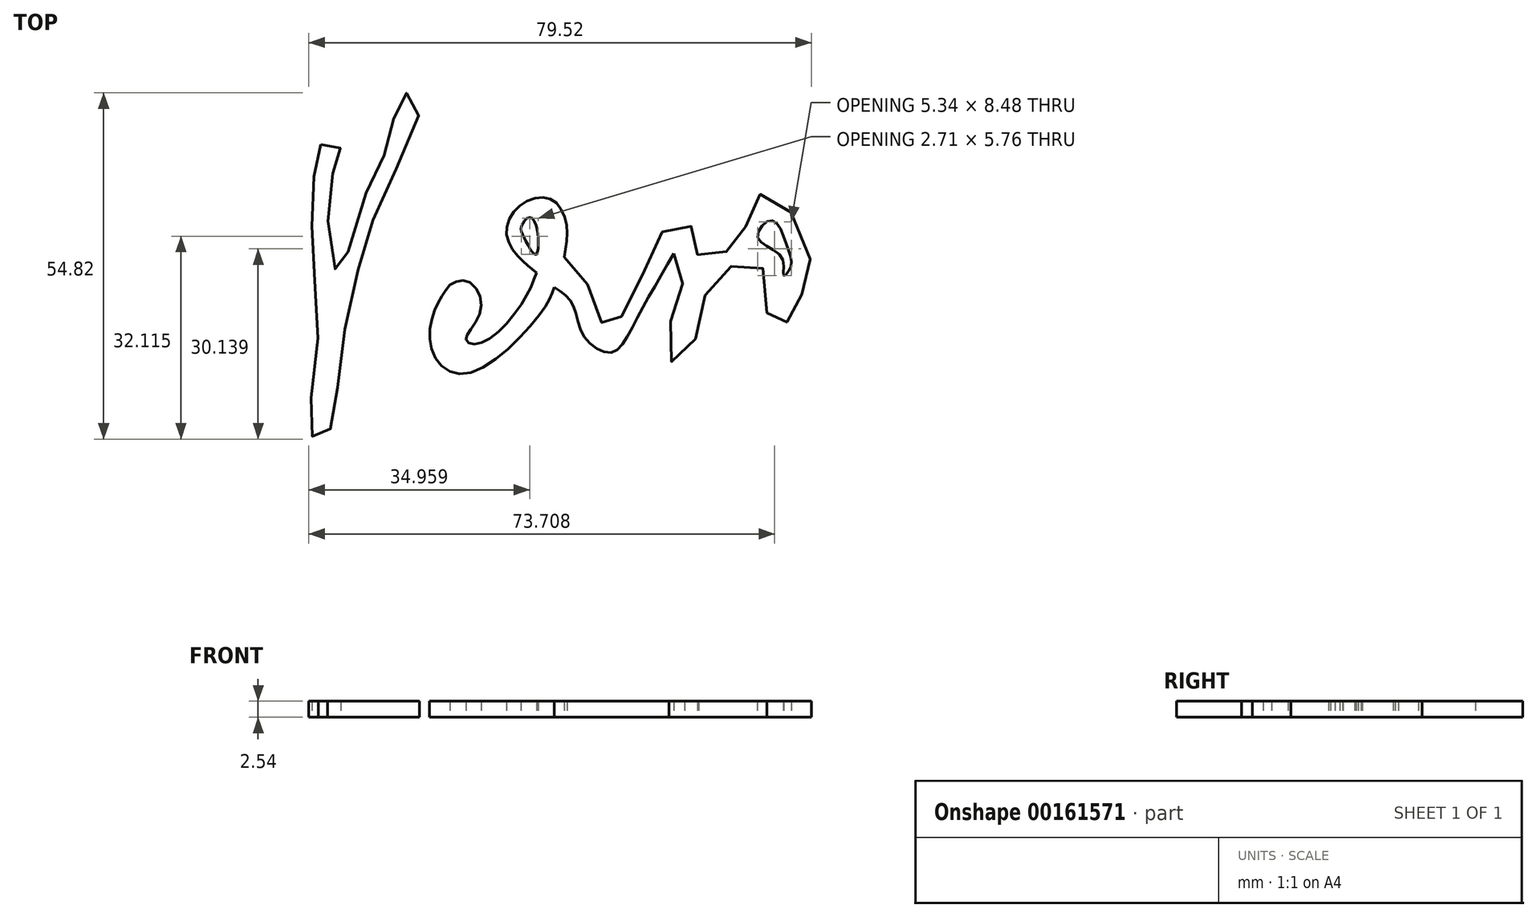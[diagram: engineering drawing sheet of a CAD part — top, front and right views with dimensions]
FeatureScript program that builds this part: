
annotation { "Feature Type Name" : "Feature", "Feature Type Description" : "" }
export const myFeature = defineFeature(function(context is Context, id is Id, definition is map)
    precondition{}
    {
        {
            var Q0;
            Q0=qCreatedBy(makeId("Top.planeOp"),FACE);
            var sketch = newSketch(context, id + "F0", { "sketchPlane" : qUnion([Q0])});
            skFitSpline(sketch, "E0", {"points": [v(-43.69, 4.8) * mm, v(-44.78, 0) * mm, v(-45.02, -11.97) * mm, v(-44.17, -26.91) * mm, v(-45.5, -40.16) * mm, v(-44.3, -41.86) * mm, v(-42.1, -40.16) * mm, v(-40.77, -30.44) * mm, v(-37.49, -13.91) * mm, v(-33.24, -2) * mm, v(-28.13, 11.12) * mm, v(-30.08, 12.94) * mm, v(-31.78, 10.4) * mm, v(-33.36, 3.83) * mm, v(-36.76, -3.58) * mm, v(-40.77, -15.5) * mm, v(-41.74, -13.79) * mm, v(-42.23, -1.15) * mm, v(-40.65, 2.62) * mm, v(-41.13, 5.17) * mm, v(-43.69, 4.8) * mm]});
            skFitSpline(sketch, "E1", {"points": [v(-23.27, -17.44) * mm, v(-25.34, -20.72) * mm, v(-26.19, -27.52) * mm, v(-20.96, -31.53) * mm, v(-8.81, -21.8) * mm, v(-6.74, -17.8) * mm], "startDerivative": vector(-14.47, -19.08) * mm, "endDerivative": vector(7.03, 20.44) * mm});
            skFitSpline(sketch, "E2", {"points": [v(-6.74, -17.8) * mm, v(-3.83, -20.47) * mm, v(-2.13, -25.46) * mm, v(2.25, -28.13) * mm, v(6.01, -23.39) * mm, v(12.21, -12.45) * mm], "startDerivative": vector(21.78, -14.05) * mm, "endDerivative": vector(23.64, 40.23) * mm});
            skFitSpline(sketch, "E3", {"points": [v(12.21, -12.45) * mm, v(13.91, -15.61) * mm, v(12.46, -19.99) * mm, v(11.48, -25.58) * mm, v(12.1, -29.83) * mm, v(15.13, -27.04) * mm, v(16.83, -20.23) * mm, v(19.14, -15.98) * mm, v(24, -13.67) * mm, v(26.55, -15.37) * mm, v(26.92, -22.17) * mm, v(27.52, -23.63) * mm, v(31.17, -22.66) * mm, v(32.26, -19.38) * mm, v(33.84, -16.1) * mm, v(32.14, -8.56) * mm, v(28.25, -3.46) * mm, v(24.97, -3.58) * mm, v(23.51, -8.32) * mm, v(22.66, -10.5) * mm, v(17.8, -13.3) * mm, v(15.98, -12.82) * mm, v(16.1, -10.5) * mm, v(14.16, -7.71) * mm, v(10.88, -8.44) * mm, v(9.05, -12.09) * mm, v(4.8, -20.47) * mm, v(2.61, -24.12) * mm, v(0.91, -23.63) * mm, v(-0.18, -19.74) * mm, v(-4.56, -13.55) * mm, v(-5.17, -13.06) * mm], "startDerivative": vector(82.26, -99.81) * mm, "endDerivative": vector(-32.12, 20.14) * mm});
            skFitSpline(sketch, "E4", {"points": [v(-5.17, -13.06) * mm, v(-4.8, -7.84) * mm, v(-7.35, -3.82) * mm, v(-12.21, -4.92) * mm, v(-14.28, -9.54) * mm, v(-11.73, -13.67) * mm, v(-9.54, -15.5) * mm], "startDerivative": vector(5.6, 29.1) * mm, "endDerivative": vector(15.71, -11.83) * mm});
            skFitSpline(sketch, "E5", {"points": [v(-9.54, -15.5) * mm, v(-11.12, -19.14) * mm, v(-15.98, -25.21) * mm, v(-19.75, -26.8) * mm, v(-20.72, -26.06) * mm, v(-19.75, -24.24) * mm, v(-18.29, -19.99) * mm, v(-20.6, -16.83) * mm, v(-23.27, -17.44) * mm], "startDerivative": vector(-9.04, -25.38) * mm, "endDerivative": vector(-24.35, -12.23) * mm});
            skFitSpline(sketch, "E6", {"points": [v(-10.23, -6.86) * mm, v(-9.54, -12.57) * mm, v(-11.36, -10.27) * mm, v(-11.85, -7.96) * mm, v(-10.23, -6.86) * mm]});
            skFitSpline(sketch, "E7", {"points": [v(25.46, -9.9) * mm, v(27.65, -7.23) * mm, v(30.08, -11.24) * mm, v(30.68, -14.64) * mm, v(29.59, -15.98) * mm, v(29.35, -13.18) * mm, v(25.46, -9.9) * mm]});
            skFitSpline(sketch, "E8", {"points": [v(78.31, -9.28) * mm, v(77.05, -12.2) * mm, v(73.37, -11.94) * mm, v(69.83, -5.86) * mm, v(69.83, -0.16) * mm, v(67.93, 1.1) * mm, v(67.93, 4.15) * mm, v(69.83, 6.43) * mm, v(69.57, 9.47) * mm, v(71.85, 24.28) * mm, v(77.93, 39.86) * mm, v(81.86, 41.13) * mm, v(84.14, 37.7) * mm, v(83.25, 25.93) * mm, v(75.9, 10.6) * mm, v(72.74, 5.8) * mm], "startDerivative": vector(-14.94, -73.82) * mm, "endDerivative": vector(-43.32, -62.37) * mm});
            skFitSpline(sketch, "E9", {"points": [v(72.74, 5.8) * mm, v(72.61, -0.41) * mm, v(74.26, -8.01) * mm, v(77.05, -8.52) * mm, v(78.44, -8.14) * mm, v(78.31, -9.28) * mm], "startDerivative": vector(-1.12, -20.77) * mm, "endDerivative": vector(-3.7, -13.08) * mm});
            skFitSpline(sketch, "E10", {"points": [v(80.21, 36.44) * mm, v(75.9, 25.93) * mm, v(73.25, 15.3) * mm, v(73.25, 12.5) * mm, v(75.4, 14.78) * mm, v(79.33, 22.9) * mm, v(81.22, 31.88) * mm, v(81.48, 36.95) * mm, v(80.21, 36.44) * mm]});
            skFitSpline(sketch, "E11", {"points": [v(95.92, 34.42) * mm, v(96.8, 32.77) * mm, v(96.55, 28.59) * mm, v(97.82, 28.2) * mm, v(99.59, 30.49) * mm, v(99.08, 32.52) * mm, v(99.08, 35.94) * mm, v(96.8, 36.32) * mm, v(95.92, 34.42) * mm]});
            skFitSpline(sketch, "E12", {"points": [v(102.88, 11.74) * mm, v(100.35, 6.05) * mm, v(99.84, -2.44) * mm, v(102.5, -4.6) * mm, v(105.8, -2.44) * mm, v(107.82, 2.63) * mm, v(108.58, 2.25) * mm, v(112, 0.35) * mm, v(115.67, 0.98) * mm, v(122, 9.34) * mm], "startDerivative": vector(-21.7, -39.66) * mm, "endDerivative": vector(39, 63) * mm});
            skFitSpline(sketch, "E13", {"points": [v(102.88, 11.74) * mm, v(102.5, 13.14) * mm, v(103.52, 13.26) * mm], "startDerivative": vector(-1.5, 3.19) * mm, "endDerivative": vector(2.88, -0.25) * mm});
            skFitSpline(sketch, "E14", {"points": [v(103.52, 13.26) * mm, v(106.94, 18.08) * mm, v(109.09, 17.82) * mm, v(109.34, 11.62) * mm, v(110.48, 6.68) * mm, v(114.28, 4.65) * mm, v(117.2, 7.82) * mm, v(120.49, 12.12) * mm], "startDerivative": vector(19.66, 38.15) * mm, "endDerivative": vector(22.24, 26.78) * mm});
            skFitSpline(sketch, "E15", {"points": [v(139.1, 26.7) * mm, v(139.06, 35.98) * mm, v(141.28, 45.9) * mm, v(143.5, 48.46) * mm, v(146.87, 48) * mm, v(147.7, 40.65) * mm, v(143.73, 28.87) * mm, v(141.86, 25.02) * mm, v(143.5, 24.79) * mm, v(147.46, 27.47) * mm, v(152.94, 29.1) * mm, v(155.39, 28.17) * mm, v(154.92, 25.84) * mm, v(153.17, 26.07) * mm, v(148.62, 24.44) * mm, v(146.64, 21.87) * mm, v(145, 21.17) * mm, v(142.56, 17.68) * mm, v(141.98, 10.1) * mm, v(139.53, 1) * mm, v(138.36, 2.29) * mm, v(136.61, 2.75) * mm, v(136.5, 9.28) * mm, v(138.36, 17.91) * mm, v(137.43, 18.6) * mm, v(132.53, 11.61) * mm, v(127.52, 7.77) * mm, v(124.49, 7.88) * mm, v(122, 9.34) * mm], "startDerivative": vector(-11.09, 174.57) * mm, "endDerivative": vector(-84.35, 59.96) * mm});
            skFitSpline(sketch, "E16", {"points": [v(104.44, 7.77) * mm, v(102.92, 2.99) * mm, v(103.15, 1.12) * mm, v(105.25, 3.45) * mm, v(106.18, 6.37) * mm, v(104.44, 7.77) * mm]});
            skFitSpline(sketch, "E17", {"points": [v(107.47, 13.48) * mm, v(106.23, 12.47) * mm, v(107.4, 10.41) * mm, v(107.47, 13.48) * mm]});
            skFitSpline(sketch, "E18", {"points": [v(126.7, 36.33) * mm, v(124.6, 33.18) * mm, v(123.2, 17.91) * mm, v(125.07, 19.9) * mm, v(129.15, 29.57) * mm, v(130.79, 34.12) * mm, v(128.8, 37.26) * mm, v(126.7, 36.33) * mm]});
            skFitSpline(sketch, "E19", {"points": [v(143.73, 39.83) * mm, v(142.44, 37.61) * mm, v(142.44, 35.4) * mm, v(144.08, 37.5) * mm, v(143.73, 39.83) * mm]});
            skFitSpline(sketch, "E20", {"points": [v(152.82, 17.56) * mm, v(150.96, 16.98) * mm, v(150.26, 11.03) * mm, v(151.77, 6.25) * mm, v(155.39, 6.6) * mm, v(157.25, 6.37) * mm, v(158.3, 8.47) * mm, v(161.57, 12.55) * mm, v(162.85, 21.4) * mm, v(165.86, 21.91) * mm, v(162.61, 24.9) * mm, v(160.98, 23.86) * mm, v(158.18, 24.2) * mm, v(154.8, 22) * mm, v(154.4, 19) * mm, v(158.65, 21.17) * mm, v(159.93, 16.98) * mm, v(155.97, 11.15) * mm, v(153.4, 11.15) * mm, v(153.4, 14.76) * mm, v(154.8, 16.28) * mm, v(154.45, 17.56) * mm, v(152.82, 17.56) * mm]});
            skFitSpline(sketch, "E21", {"points": [v(139.1, 26.7) * mm, v(134.3, 19.3) * mm, v(128.9, 12.54) * mm, v(125.65, 11.96) * mm, v(125.07, 13.65) * mm, v(128.45, 21.51) * mm, v(132.16, 28.6) * mm, v(133.4, 36.86) * mm, v(129.36, 40.5) * mm, v(124.55, 38.62) * mm, v(120.71, 26.98) * mm, v(120.71, 17.87) * mm, v(120.49, 12.12) * mm], "startDerivative": vector(-49.65, -75.15) * mm, "endDerivative": vector(-6.3, -71.96) * mm});
            skSolve(sketch);
        }
        {
            var Q0;
            Q0=makeQuery(id+"F0.imprint","IMPRINT",FACE,{"disambiguationData":[TD([[makeQuery(id+"F0.imprint","IMPRINT",EDGE,{"derivedFrom":sQuery(id+"F0.wireOp",EDGE,"E0")}),1.0]])]});
            var Q1;
            Q1=makeQuery(id+"F0.imprint","IMPRINT",FACE,{"disambiguationData":[TD([[makeQuery(id+"F0.imprint","IMPRINT",EDGE,{"derivedFrom":sQuery(id+"F0.wireOp",EDGE,"E1")}),1.0]])]});
            extrude(context, id + "F1", {"entities" : qUnion([Q0, Q1]), "depth" : 2.54 * mm});
        }
    });
